# Revit family: DIVITYP018
name_source: partatom
category: Furniture
units: mm (PartAtom-declared; Revit-internal decimal feet)

## family parameters
Always vertical = Yes
Cut with Voids When Loaded = No
OmniClass Number = 23.40.20.00
OmniClass Title = General Furniture and Specialties
Render Appearance Source = Family Geometry
Room Calculation Point = No
Shared = No
Work Plane-Based = No

## types (1)
- DIVITYP018
    Cost = 80103 $
    Default Elevation = 0 mm  [stored 0 ft]
    Description = 6 x Upton - Black Mesh Back - Black Seat Fabric, 6 x 24 Led Task Light, W/ Dimmer & Transformer, 6 x Snap-In Data Plate w/6 Gang Face - Black, 3 x Black Duplex Outlet - Line 1, 3 x Black Duplex Outlet - Line 2, 3 x Black Duplex Outlet - Line 3, 3 x Black Duplex Outlet - Line 4 - Dedicated, 2 x 57 in. Electrical Jumper  (Pt 36E & Vt 48), 1 x 21 in. Electrical Jumper  (Extended Panel To Panel), 1 x LH Receptacle Mounted Base Infeed - 72L - 8 Wire, 4 Circuit, 2 x DiVi LINEAR BASE RACEWAY SHROUD 3-WAY 90 DEGREES, 6 x DiVi LINEAR BASE RACEWAY SHROUD 2-WAY 90 DEGREES, 4 x DiVi LINEAR HARD PANEL-PWR-PERM MONO- 66H X 36W, 10 x DiVi LINEAR Hard PANEL -NPWR-PERM MONO- 66H X 36W, 6 x DiVi LINEAR QTR GLASS PANEL -NPWR- PERM MONO 66H X 30W, 8 x DiVi LINEAR QTR GLASS PANEL -NPWR- PERM MONO 66H X 36W, 8 x DIVI LINEAR BASE RACEWAY SHROUD END OF RUN, 6 x Type C Flipper Unit - Laminate Face - 36W, 6 x Pedestal - F/F - 24D, 6 x Rectangular - 2mm Edge - 24D x 42W, 6 x Rectangular - 2mm Edge - 30D x 72W, 18 x Flat Plate, 3 x Regular Cantilever - Left Hand - 24D, 3 x Regular Cantilever - Right Hand - 24D, 11 x Regular Cantilever - Left Hand - 30D, 7 x Regular Cantilever - Right Hand - 30D
    Exported From CET Designer = Yes
    Manufacturer = AIS
    Model = 4700
    Show DIVITYP018 = Yes
    VisibilityIndex = 0

note: [stored X ft] marks values corroborated as IEEE doubles in the binary element streams (Revit-internal decimal feet)

## geometry (parser evidence)
native form markers: Sweep x2
no freeform markers — native parametric forms only
